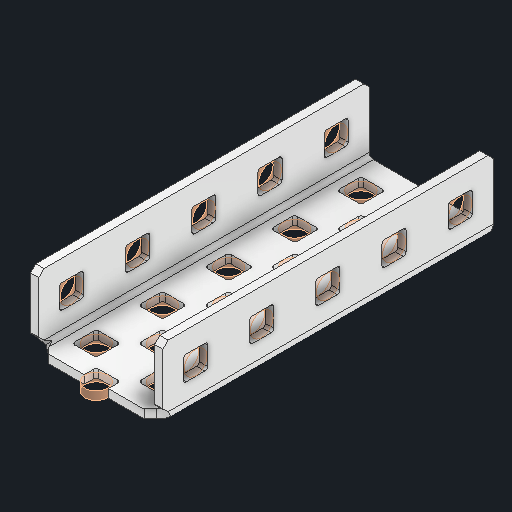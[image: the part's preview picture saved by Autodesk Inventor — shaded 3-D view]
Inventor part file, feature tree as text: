
AUTODESK INVENTOR PART (.ipt)
format: ipt  version: 2024 (Build 280153000, 153)  size: 571,392 bytes
history: native  units: in
note: dims shown in document units (in); Inventor stores cm internally (conversion verified against a paired STEP export)
features: other x56, sketch x5, sheet_metal_op x1
ambient origin geometry x8: Origin, YZ Plane, XZ Plane, XY Plane, X Axis, Y Axis, Z Axis, Center Point
bodies: Solid1 (feature_tree)
feature tree (62):
  other  "Alu C 1x2x1x5.ipt"
  other  "Solid1::Alu C 1x2x1x5.ipt"
  other  "TaggingFeature1"
  sketch  "Sketch1"  dims[d0=0.3937in]
  sketch  "Sketch2"  dims[d1=0.0625in]
  sketch  "Sketch3"
  other  "Flange Pattern Sketch"
  sketch  "Sketch9"
  sheet_metal_op  "Body Pattern Sketch"
  other  "Arc Length"
  sketch  "Sketch14"
  other  "Flange Pattern Plane"
  other  "Srf1"
  other  "Srf2"
  other  "Srf3"
  other  "Srf4"
  other  "Srf5"
  other  "Srf6"
  other  "Srf7"
  other  "Srf8"
  other  "Srf9"
  other  "Srf10"
  other  "Srf11"
  other  "Srf12"
  other  "Srf13"
  other  "Srf14"
  other  "Srf15"
  other  "Srf16"
  other  "Srf17"
  other  "Srf18"
  other  "Srf19"
  other  "Srf20"
  other  "Srf21"
  other  "Srf22"
  other  "Srf23"
  other  "Srf24"
  other  "Srf25"
  other  "Srf1::Derived"
  other  "Srf2::Derived"
  other  "Srf823::Derived"
  other  "Srf824::Derived"
  other  "Srf825::Derived"
  other  "Srf826::Derived"
  other  "Srf827::Derived"
  other  "Srf828::Derived"
  other  "Srf829::Derived"
  other  "Srf922::Derived"
  other  "Srf91::Derived"
  other  "Srf92::Derived"
  other  "Srf856::Derived"
  other  "Srf857::Derived"
  other  "Srf858::Derived"
  other  "Srf859::Derived"
  other  "Srf860::Derived"
  other  "Srf861::Derived"
  other  "Srf862::Derived"
  other  "Srf959::Derived"
  other  "Srf786::Derived"
  other  "Srf889::Derived"
  other  "Srf890::Derived"
  other  "Srf891::Derived"
  other  "Srf892::Derived"
